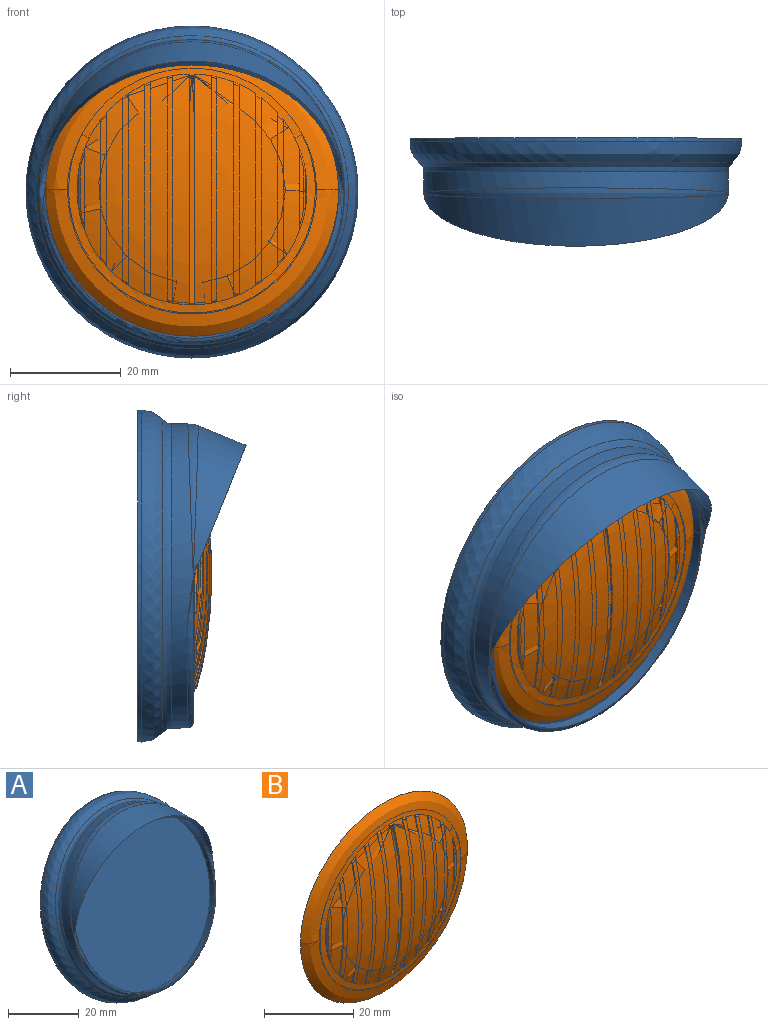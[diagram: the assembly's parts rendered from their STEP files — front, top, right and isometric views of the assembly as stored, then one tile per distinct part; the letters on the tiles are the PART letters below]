
ASSEMBLY  parts=2 mates=1
PART A: 21 faces, bbox 72.7x44x69.7 mm
  f0: plane 1.43x0.58mm, normal (0,-0.93,0.37), area 0mm2, adj f10,f16,f18
  f1: plane 53x24.57mm, normal (0,-0.93,0.37), area 0.8mm2, adj f9,f16
  f2: cylinder r=30mm len=60mm, axis (0,-0.93,0.37), area 126.3mm2, adj f3,f14
  f3: plane 60x55.63mm, normal (0,0.93,-0.37), area 2827.4mm2, adj f2
  f4: cylinder r=27.5mm len=55mm, axis (0,0.93,-0.37), area 550.3mm2, adj f7,f13,f15,f16,f17,f19
  f5: plane 1.43x0.58mm, normal (0,-0.93,0.37), area 0mm2, adj f10,f16,f20
  f6: extruded ~50x15.7mm, area 0mm2, adj f8,f12
  f7: extruded ~54.99x25.95mm, area 499mm2, adj f4,f12,f13,f17,f19
  f8: plane 63.45x29.53mm, normal (0,0.93,-0.37), area 6.5mm2, adj f6,f10,f12
  f9: extruded ~53x25.3mm, area 166.4mm2, adj f1,f10,f11
  f10: extruded ~53x24.73mm, area 168.5mm2, adj f0,f5,f8,f9,f11,f12,f18,f20
  f11: plane 53x48.2mm, normal (0,-0.93,0.37), area 2163.7mm2, adj f9,f10
  f12: bspline ~55.02x26.84mm, area 284.8mm2, adj f6,f7,f8,f10,f17,f18,f19,f20
  f13: bspline ~55x25.5mm, area 0mm2, adj f4,f7
  f14: bspline ~59.95x56mm, area 805.7mm2, adj f2,f15
  f15: bspline ~56.52x52.39mm, area 312mm2, adj f4,f14
  f16: torus R=26.5mm, axis (0,-0.93,0.37), area 123.7mm2, adj f0,f1,f4,f5,f17,f19
  f17: bspline ~11.85x3.23mm, area 5.3mm2, adj f4,f7,f12,f16,f18
  f18: bspline ~8.64x3.94mm, area 3.7mm2, adj f0,f10,f12,f17
  f19: bspline ~11.85x3.23mm, area 5.3mm2, adj f4,f7,f12,f16,f20
  f20: bspline ~7.12x3.38mm, area 3.7mm2, adj f5,f10,f12,f19
PART B: 92 faces, bbox 55.1x7.4x54.1 mm
  f0: bspline ~1.62x1.41mm, area 0.8mm2, adj f1,f89,f90,f91
  f1: bspline ~44.55x32.25mm, area 133mm2, adj f0,f2,f6,f55,f61,f62,f63,f64
  f2: plane 45.03x32.49mm, normal (0,-1,0), area 17.3mm2, adj f1,f3,f5
  f3: bspline ~53.02x28.08mm, area 359mm2, adj f2,f4,f5
  f4: plane 53.79x52.78mm, normal (0,1,0), area 2163.7mm2, adj f3,f5
  f5: bspline ~53.01x28.13mm, area 351.9mm2, adj f2,f3,f4,f6
  f6: bspline ~39.85x12.65mm, area 59.4mm2, adj f1,f5,f7,f13,f14,f20,f26,f32
  f7: extruded ~0.57x0.44mm, area 0mm2, adj f6,f8
  f8: bspline ~2.03x1.64mm, area 0.6mm2, adj f7,f9,f11,f12,f13
  f9: plane 33.36x2.3mm, normal (1,0,0), area 10.2mm2, adj f8,f10,f11,f77,f78
  f10: bspline ~1.68x1.31mm, area 0.6mm2, adj f9,f11,f12,f77
  f11: revolved ~34.05x14.12mm, area 34mm2, adj f8,f9,f10,f12
  f12: plane 34.77x2.44mm, normal (-1,0,0), area 10.6mm2, adj f8,f10,f11,f76,f77
  f13: extruded ~0.43x0.28mm, area 0mm2, adj f6,f8
  f14: plane 1.01x0.44mm, normal (0.39,0,0.92), area 0mm2, adj f6,f15,f18,f19
  f15: plane 38.07x2.76mm, normal (1,0,0), area 11.6mm2, adj f14,f16,f17,f18,f75,f76
  f16: bspline ~5.63x2.56mm, area 0.6mm2, adj f15,f17,f19,f75
  f17: revolved ~38.33x17.85mm, area 38.4mm2, adj f15,f16,f18,f19
  f18: bspline ~5.59x2.59mm, area 0.6mm2, adj f14,f15,f17,f19
  f19: plane 38.91x2.85mm, normal (-1,0,0), area 11.8mm2, adj f14,f16,f17,f18,f74,f75
  f20: plane 1.01x0.21mm, normal (0.2,0,0.98), area 0mm2, adj f6,f21,f24,f25
  f21: plane 40.72x3.03mm, normal (1,0,0), area 12.4mm2, adj f20,f22,f23,f24,f73,f74
  f22: bspline ~5.92x1.43mm, area 0.5mm2, adj f21,f23,f25,f73
  f23: revolved ~40.63x20.02mm, area 40.9mm2, adj f21,f22,f24,f25
  f24: bspline ~5.89x1.45mm, area 0.5mm2, adj f20,f21,f23,f25
  f25: plane 41.12x3.07mm, normal (-1,0,0), area 12.5mm2, adj f20,f22,f23,f24,f72,f73
  f26: plane 1.01x0.03mm, normal (0,0,1), area 0mm2, adj f6,f27,f30,f31
  f27: plane 41.69x3.11mm, normal (1,0,0), area 12.6mm2, adj f26,f28,f29,f30,f71,f72
  f28: bspline ~6.15x0.45mm, area 0.5mm2, adj f27,f29,f31,f71
  f29: revolved ~41.25x41.25mm, area 41.7mm2, adj f27,f28,f30,f31
  f30: bspline ~6.11x0.45mm, area 0.5mm2, adj f26,f27,f29,f31
  f31: plane 41.69x3.11mm, normal (-1,0,0), area 12.6mm2, adj f26,f28,f29,f30,f70,f71
  f32: plane 1.01x0.21mm, normal (-0.2,0,0.98), area 0mm2, adj f6,f33,f36,f37
  f33: plane 41.12x3.07mm, normal (1,0,0), area 12.5mm2, adj f32,f34,f35,f36,f69,f70
  f34: bspline ~5.92x1.43mm, area 0.5mm2, adj f33,f35,f37,f69
  f35: revolved ~40.63x20.02mm, area 40.9mm2, adj f33,f34,f36,f37
  f36: bspline ~5.89x1.45mm, area 0.5mm2, adj f32,f33,f35,f37
  f37: plane 40.72x3.03mm, normal (-1,0,0), area 12.4mm2, adj f32,f34,f35,f36,f68,f69
  f38: plane 1.01x0.44mm, normal (-0.39,0,0.92), area 0mm2, adj f6,f39,f42,f43
  f39: plane 38.91x2.85mm, normal (1,0,0), area 11.8mm2, adj f38,f40,f41,f42,f67,f68
  f40: bspline ~5.63x2.56mm, area 0.6mm2, adj f39,f41,f43,f67
  f41: revolved ~38.33x17.85mm, area 38.4mm2, adj f39,f40,f42,f43
  f42: bspline ~5.59x2.59mm, area 0.6mm2, adj f38,f39,f41,f43
  f43: plane 38.07x2.76mm, normal (-1,0,0), area 11.6mm2, adj f38,f40,f41,f42,f66,f67
  f44: extruded ~1x0.71mm, area 0mm2, adj f6,f45
  f45: bspline ~1.8x1.42mm, area 0.6mm2, adj f44,f46,f48,f49
  f46: plane 34.77x2.44mm, normal (1,0,0), area 10.6mm2, adj f45,f47,f48,f65,f66
  f47: bspline ~1.63x1.29mm, area 0.6mm2, adj f46,f48,f49,f65
  f48: revolved ~34.05x14.12mm, area 34mm2, adj f45,f46,f47,f49
  f49: plane 33.36x2.3mm, normal (-1,0,0), area 10.2mm2, adj f45,f47,f48,f64,f65
  f50: bspline ~1.71x1.44mm, area 0.8mm2, adj f6,f89,f90,f91
  f51: bspline ~1.71x1.44mm, area 0.8mm2, adj f6,f52,f53,f54
  f52: revolved ~26.88x8.82mm, area 26.4mm2, adj f51,f53,f54,f79
  f53: plane 27.88x1.83mm, normal (-1,0,0), area 8.2mm2, adj f51,f52,f78,f79
  f54: plane 25.44x1.6mm, normal (1,0,0), area 7.3mm2, adj f51,f52,f79,f80
  f55: bspline ~3.8x1.26mm, area 1.8mm2, adj f1,f56,f58,f60
  f56: revolved ~12.71x1.03mm, area 0mm2, adj f55,f57,f58,f60
  f57: bspline ~5.31x1.62mm, area 1.8mm2, adj f56,f58,f60,f62
  f58: bspline ~9.83x0.56mm, area 3.5mm2, adj f55,f56,f57,f59
  f59: plane 7.49x0.71mm, normal (-1,0,0), area 0mm2, adj f58,f61
  f60: plane 16.51x2.8mm, normal (1,0,0), area 4.1mm2, adj f55,f56,f57,f63
  f61: revolved ~6.88x0.29mm, area 0mm2, adj f1,f59
  f62: extruded ~3.76x1mm, area 0mm2, adj f1,f57
  f63: revolved ~25.3x7.7mm, area 63.7mm2, adj f1,f6,f60,f89
  f64: revolved ~33.29x13.32mm, area 94.3mm2, adj f1,f6,f49,f91
  f65: extruded ~1x0.71mm, area 0mm2, adj f1,f46,f47,f49
  f66: revolved ~38.09x17.4mm, area 111.5mm2, adj f1,f6,f43,f46
  f67: plane 1.01x0.43mm, normal (-0.38,0,-0.92), area 0mm2, adj f1,f39,f40,f43
  f68: revolved ~40.8x19.93mm, area 121.4mm2, adj f1,f6,f37,f39
  f69: plane 1.01x0.21mm, normal (-0.19,0,-0.98), area 0mm2, adj f1,f33,f34,f37
  f70: revolved ~41.81x20.9mm, area 126mm2, adj f1,f6,f31,f33
  f71: plane 1.01x0.03mm, normal (0,0,-1), area 0mm2, adj f1,f27,f28,f31
  f72: revolved ~41.81x20.9mm, area 126.1mm2, adj f1,f6,f25,f27
  f73: plane 1.01x0.21mm, normal (0.19,0,-0.98), area 0mm2, adj f1,f21,f22,f25
  f74: revolved ~40.8x19.93mm, area 121.3mm2, adj f1,f6,f19,f21
  f75: plane 1.01x0.43mm, normal (0.38,0,-0.92), area 0mm2, adj f1,f15,f16,f19
  f76: revolved ~38.09x17.4mm, area 111.4mm2, adj f1,f6,f12,f15
  f77: extruded ~1x0.71mm, area 0mm2, adj f1,f9,f10,f12
  f78: revolved ~33.29x13.32mm, area 95.1mm2, adj f1,f6,f9,f53
  f79: bspline ~2.61x2.25mm, area 0.8mm2, adj f1,f52,f53,f54
  f80: revolved ~25.3x7.7mm, area 63.7mm2, adj f1,f6,f54,f81
  f81: plane 16.51x2.8mm, normal (-1,0,0), area 4.1mm2, adj f80,f82,f85,f88
  f82: revolved ~12.71x1.03mm, area 0mm2, adj f81,f83,f85,f88
  f83: bspline ~9.83x0.56mm, area 3.5mm2, adj f82,f84,f85,f88
  f84: plane 7.49x0.71mm, normal (1,0,0), area 0mm2, adj f83,f87
  f85: bspline ~5.31x1.62mm, area 1.8mm2, adj f81,f82,f83,f86
  f86: extruded ~3.76x1mm, area 0mm2, adj f1,f85
  f87: revolved ~6.88x0.29mm, area 0mm2, adj f1,f84
  f88: bspline ~3.8x1.26mm, area 1.8mm2, adj f1,f81,f82,f83
  f89: plane 25.44x1.6mm, normal (-1,0,0), area 7.3mm2, adj f0,f50,f63,f90
  f90: revolved ~26.88x8.82mm, area 26.4mm2, adj f0,f50,f89,f91
  f91: plane 27.89x1.84mm, normal (1,0,0), area 8.2mm2, adj f0,f50,f64,f90
PLACE A rot(axis=(1,0,0),22deg) t=(-59.19,-18.49,14.41)mm
PLACE B t=(-59.19,-21.49,14.83)mm
MATE fastened A.f4 <-> B.f4  axis (0,-1,0) through (-59.19,-21.49,14.41)mm
